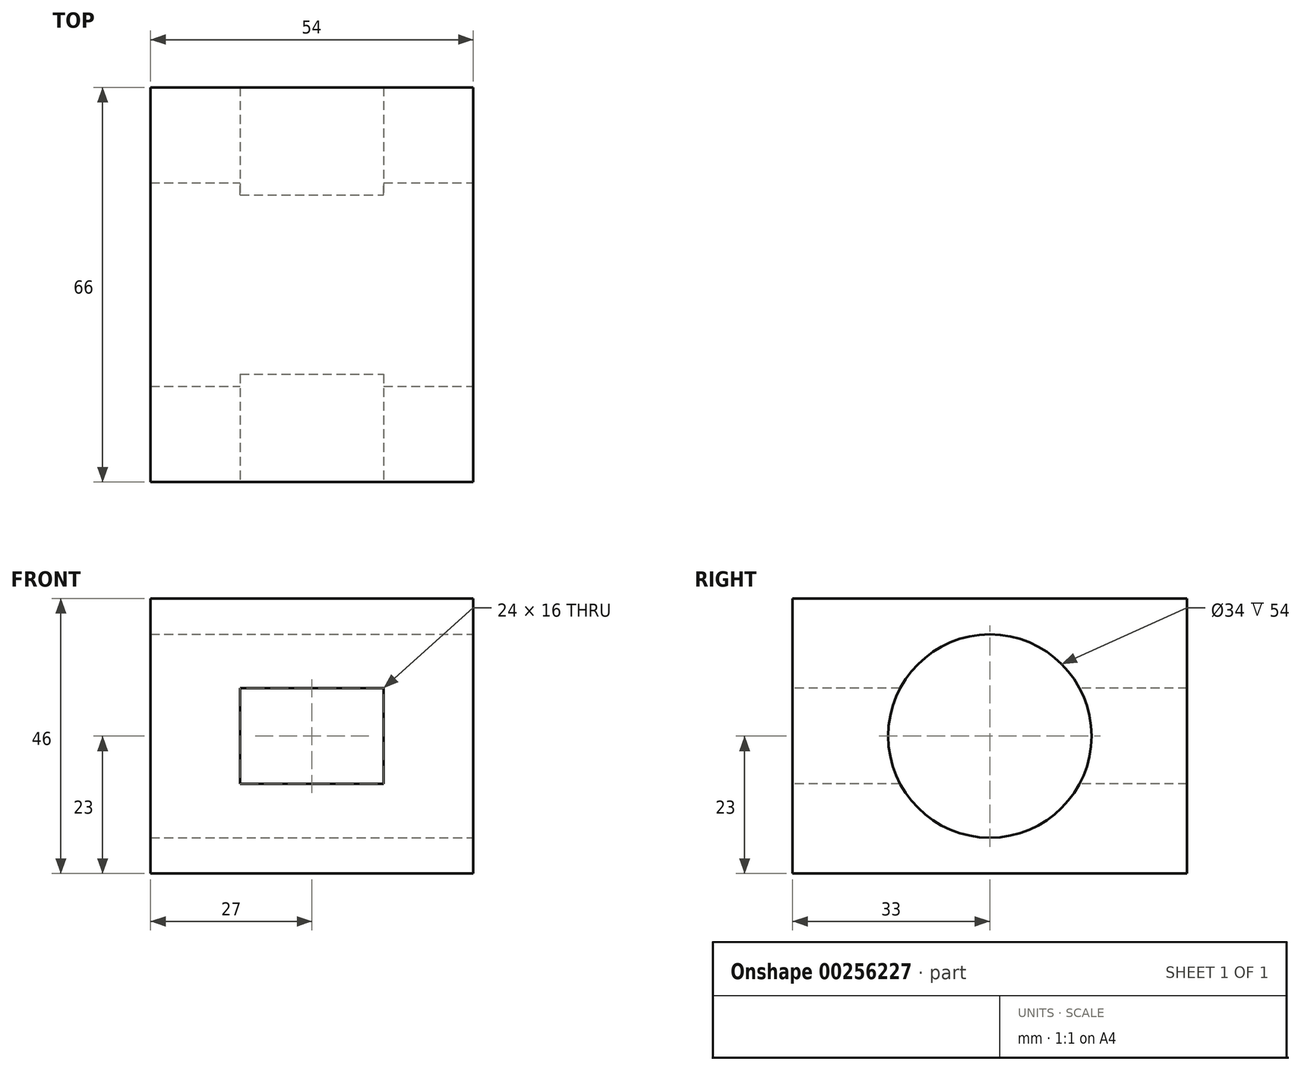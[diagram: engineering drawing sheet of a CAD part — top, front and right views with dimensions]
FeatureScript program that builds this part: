
annotation { "Feature Type Name" : "Feature", "Feature Type Description" : "" }
export const myFeature = defineFeature(function(context is Context, id is Id, definition is map)
    precondition{}
    {
        {
            var Q0;
            Q0=qCreatedBy(makeId("Top.planeOp"),FACE);
            var sketch = newSketch(context, id + "F0", { "sketchPlane" : qUnion([Q0])});
            skLineSegment(sketch, "E0.bottom", {"start": v(0, 0) * mm, "end": v(54, 0) * mm});
            skLineSegment(sketch, "E0.top", {"start": v(0, 66) * mm, "end": v(54, 66) * mm});
            skLineSegment(sketch, "E0.left", {"start": v(0, 0) * mm, "end": v(0, 66) * mm});
            skLineSegment(sketch, "E0.right", {"start": v(54, 0) * mm, "end": v(54, 66) * mm});
            skSolve(sketch);
        }
        {
            var Q0;
            Q0=makeQuery(id+"F0.imprint","IMPRINT",FACE,{"disambiguationData":[TD([[makeQuery(id+"F0.imprint","IMPRINT",EDGE,{"derivedFrom":sQuery(id+"F0.wireOp",EDGE,"E0.bottom")}),1.0]])]});
            extrude(context, id + "F1", {"entities" : qUnion([Q0]), "depth" : 46 * mm});
        }
        {
            var Q0;
            Q0=makeQuery(id+"F1.opExtrude","SWEPT_FACE",FACE,{"disambiguationData":[OSD([sQuery(id+"F0.wireOp",EDGE,"E0.bottom")])]});
            var sketch = newSketch(context, id + "F2", { "sketchPlane" : qUnion([Q0])});
            skLineSegment(sketch, "E1.bottom", {"start": v(15, 31) * mm, "end": v(39, 31) * mm});
            skLineSegment(sketch, "E1.top", {"start": v(15, 15) * mm, "end": v(39, 15) * mm});
            skLineSegment(sketch, "E1.left", {"start": v(15, 31) * mm, "end": v(15, 15) * mm});
            skLineSegment(sketch, "E1.right", {"start": v(39, 31) * mm, "end": v(39, 15) * mm});
            skSolve(sketch);
        }
        {
            var Q0;
            Q0=makeQuery(id+"F2.imprint","IMPRINT",FACE,{"disambiguationData":[TD([[makeQuery(id+"F2.imprint","IMPRINT",EDGE,{"derivedFrom":sQuery(id+"F2.wireOp",EDGE,"E1.bottom")}),-1.0]])]});
            extrude(context, id + "F3", {"entities" : qUnion([Q0]), "operationType" : NewBodyOperationType.REMOVE, "oppositeDirection" : true, "depth" : 66 * mm});
        }
        {
            var Q0;
            Q0=makeQuery(id+"F1.opExtrude","SWEPT_FACE",FACE,{"disambiguationData":[OSD([sQuery(id+"F0.wireOp",EDGE,"E0.right")])]});
            var sketch = newSketch(context, id + "F4", { "sketchPlane" : qUnion([Q0])});
            skCircle(sketch, "E2", {"center": v(33, 23) * mm, "radius": 17 * mm});
            skSolve(sketch);
        }
        {
            var Q0;
            Q0=makeQuery(id+"F4.imprint","IMPRINT",FACE,{"disambiguationData":[TD([[makeQuery(id+"F4.imprint","IMPRINT",EDGE,{"derivedFrom":sQuery(id+"F4.wireOp",EDGE,"E2")}),1.0]])]});
            extrude(context, id + "F5", {"entities" : qUnion([Q0]), "operationType" : NewBodyOperationType.REMOVE, "oppositeDirection" : true, "depth" : 54 * mm});
        }
    });
